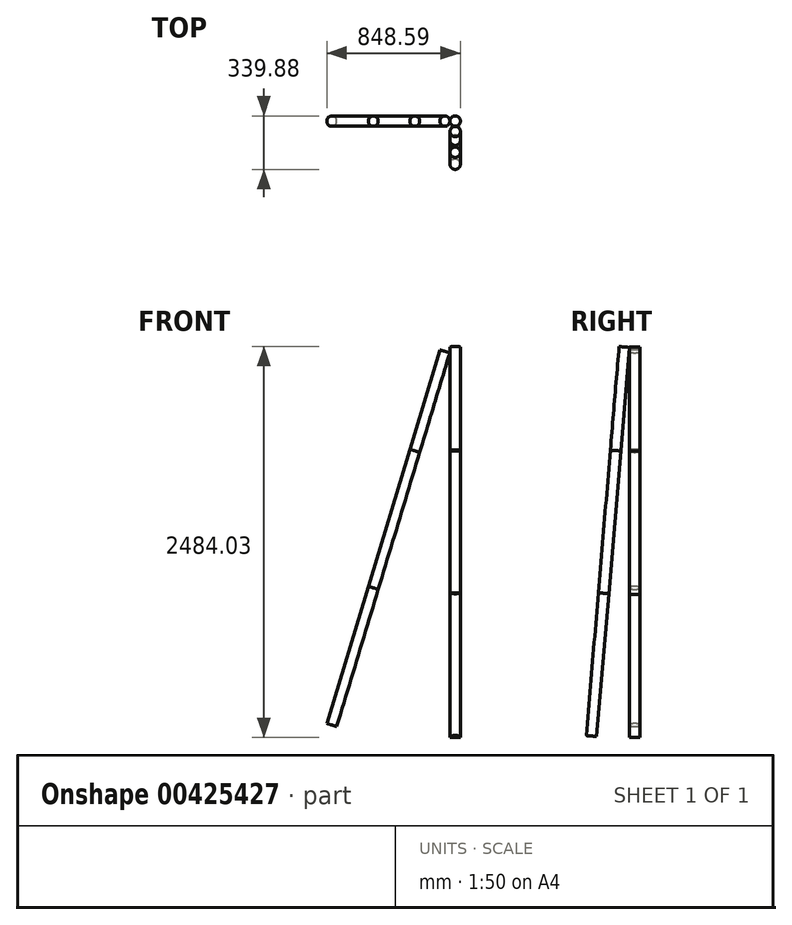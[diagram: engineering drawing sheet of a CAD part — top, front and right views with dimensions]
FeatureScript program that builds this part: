
annotation { "Feature Type Name" : "Feature", "Feature Type Description" : "" }
export const myFeature = defineFeature(function(context is Context, id is Id, definition is map)
    precondition{}
    {
        {
            assignVariable(context, id + "F0", {"name" : "A0RollLength", "anyValue" : 910 * mm});
        }
        {
            assignVariable(context, id + "F1", {"name" : "A1RollLength", "anyValue" : 660 * mm});
        }
        {
            var Q0;
            Q0=qCreatedBy(makeId("Top.planeOp"),FACE);
            var sketch = newSketch(context, id + "F2", { "sketchPlane" : qUnion([Q0])});
            skLineSegment(sketch, "E0.bottom", {"start": v(-465, 200) * mm, "end": v(465, 200) * mm});
            skLineSegment(sketch, "E0.top", {"start": v(-465, -200) * mm, "end": v(465, -200) * mm});
            skLineSegment(sketch, "E0.left", {"start": v(-465, 200) * mm, "end": v(-465, -200) * mm});
            skLineSegment(sketch, "E0.right", {"start": v(465, 200) * mm, "end": v(465, -200) * mm});
            skPoint(sketch, "E1", {"position": v(0, 200) * mm});
            skPoint(sketch, "E2", {"position": v(-465, 0) * mm});
            skCircle(sketch, "E3", {"center": v(392, 137) * mm, "radius": 33 * mm, "construction": true});
            skCircle(sketch, "E4", {"center": v(-402, 137) * mm, "radius": 33 * mm, "construction": true});
            skCircle(sketch, "E5", {"center": v(-402, -137) * mm, "radius": 33 * mm, "construction": true});
            skCircle(sketch, "E6", {"center": v(392, -137) * mm, "radius": 33 * mm, "construction": true});
            skLineSegment(sketch, "E7", {"start": v(-402, 137) * mm, "end": v(392, 137) * mm, "construction": true});
            skLineSegment(sketch, "E8", {"start": v(392, 137) * mm, "end": v(392, -137) * mm, "construction": true});
            skSolve(sketch);
        }
        {
            var Q0;
            Q0=sQuery(id+"F2.wireOp",EDGE,"E8");
            cPoint(context, id + "F3", {"entities" : qUnion([Q0]), "parameter" : 0.5});
        }
        {
            var Q0;
            Q0 = qCreatedBy(id + "F3" ,VERTEX);
            var Q1;
            Q1=qCreatedBy(makeId("Right.planeOp"),FACE);
            cPlane(context, id + "F4", {"entities" : qUnion([Q0, Q1]), "cplaneType" : CPlaneType.PLANE_POINT, "offset" : 253 * mm, "width" : 150 * mm, "height" : 150 * mm});
        }
        {
            var Q0;
            Q0=qCreatedBy(makeId("Front.planeOp"),FACE);
            var Q1;
            Q1=sQuery(id+"F2.wireOp",VERTEX,"E3.center");
            cPlane(context, id + "F5", {"entities" : qUnion([Q0, Q1]), "cplaneType" : CPlaneType.PLANE_POINT, "offset" : 25 * mm, "width" : 150 * mm, "height" : 150 * mm});
        }
        {
            var Q0;
            Q0=qCreatedBy(id+"F5.planeOp",FACE);
            var sketch = newSketch(context, id + "F6", { "sketchPlane" : qUnion([Q0])});
            skPoint(sketch, "E9.0", {"position": v(392, 0) * mm});
            skLineSegment(sketch, "E10", {"start": v(392, 0) * mm, "end": v(392, 2480) * mm, "construction": true});
            skPoint(sketch, "E11.0", {"position": v(-402, 0) * mm});
            skLineSegment(sketch, "E12", {"start": v(-392, 80) * mm, "end": v(326, 2453.79) * mm, "construction": true});
            skLineSegment(sketch, "E13", {"start": v(-423.59, 89.55) * mm, "end": v(-360.41, 70.45) * mm, "construction": true});
            skLineSegment(sketch, "E14", {"start": v(-435, 0) * mm, "end": v(-369, 0) * mm, "construction": true});
            skPoint(sketch, "E15", {"position": v(-363.28, 71.31) * mm});
            skSolve(sketch);
        }
        {
            var Q0;
            Q0=qCreatedBy(id+"F4.planeOp",FACE);
            var sketch = newSketch(context, id + "F7", { "sketchPlane" : qUnion([Q0])});
            skPoint(sketch, "E16.0", {"position": v(137, 0) * mm});
            skPoint(sketch, "E17.0", {"position": v(137, 2480) * mm});
            skPoint(sketch, "E18.0", {"position": v(-137, 0) * mm});
            skLineSegment(sketch, "E19", {"start": v(-137, 10) * mm, "end": v(71, 2481.26) * mm, "construction": true});
            skLineSegment(sketch, "E20", {"start": v(-169.88, 12.77) * mm, "end": v(-104.12, 7.23) * mm, "construction": true});
            skPoint(sketch, "E21", {"position": v(-107.1, 7.48) * mm});
            skSolve(sketch);
        }
        {
            var Q0;
            Q0=sQuery(id+"F6.wireOp",VERTEX,"E12.start");
            var Q1;
            Q1=sQuery(id+"F6.wireOp",EDGE,"E12");
            cPlane(context, id + "F8", {"entities" : qUnion([Q0, Q1]), "cplaneType" : CPlaneType.LINE_POINT, "offset" : 25 * mm, "width" : 150 * mm, "height" : 150 * mm});
        }
        {
            var Q0;
            Q0=sQuery(id+"F7.wireOp",EDGE,"E19");
            var Q1;
            Q1=sQuery(id+"F7.wireOp",VERTEX,"E19.start");
            cPlane(context, id + "F9", {"entities" : qUnion([Q0, Q1]), "cplaneType" : CPlaneType.LINE_POINT, "offset" : 25 * mm, "width" : 150 * mm, "height" : 150 * mm});
        }
        {
            var Q0;
            Q0=qCreatedBy(id+"F8.planeOp",FACE);
            var sketch = newSketch(context, id + "F10", { "sketchPlane" : qUnion([Q0])});
            skCircle(sketch, "E22", {"center": v(-398.37, 137) * mm, "radius": 33 * mm});
            skSolve(sketch);
        }
        {
            var Q0;
            Q0=makeQuery(id+"F10.imprint","IMPRINT",FACE,{"disambiguationData":[TD([[makeQuery(id+"F10.imprint","IMPRINT",EDGE,{"derivedFrom":sQuery(id+"F10.wireOp",EDGE,"E22")}),1.0]])]});
            extrude(context, id + "F11", {"entities" : qUnion([Q0]), "depth" : getVariable(context, 'A0RollLength')});
        }
        {
            var Q0;
            Q0=qCreatedBy(id+"F9.planeOp",FACE);
            var sketch = newSketch(context, id + "F12", { "sketchPlane" : qUnion([Q0])});
            skCircle(sketch, "E23", {"center": v(392, -137.36) * mm, "radius": 33 * mm});
            skSolve(sketch);
        }
        {
            var Q0;
            Q0=makeQuery(id+"F12.imprint","IMPRINT",FACE,{"disambiguationData":[TD([[makeQuery(id+"F12.imprint","IMPRINT",EDGE,{"derivedFrom":sQuery(id+"F12.wireOp",EDGE,"E23")}),1.0]])]});
            extrude(context, id + "F13", {"entities" : qUnion([Q0]), "depth" : getVariable(context, 'A0RollLength')});
        }
        {
            var Q0;
            Q0=qCreatedBy(makeId("Top.planeOp"),FACE);
            var sketch = newSketch(context, id + "F14", { "sketchPlane" : qUnion([Q0])});
            skCircle(sketch, "E24", {"center": v(392, 137) * mm, "radius": 33 * mm});
            skSolve(sketch);
        }
        {
            var Q0;
            Q0=makeQuery(id+"F14.imprint","IMPRINT",FACE,{"disambiguationData":[TD([[makeQuery(id+"F14.imprint","IMPRINT",EDGE,{"derivedFrom":sQuery(id+"F14.wireOp",EDGE,"E24")}),1.0]])]});
            extrude(context, id + "F15", {"entities" : qUnion([Q0]), "depth" : getVariable(context, 'A0RollLength')});
        }
        {
            var Q0;
            Q0=qCreatedBy(makeId("Top.planeOp"),FACE);
            cPlane(context, id + "F16", {"entities" : qUnion([Q0]), "cplaneType" : CPlaneType.OFFSET, "offset" : getVariable(context, 'A1RollLength'), "width" : 150 * mm, "height" : 150 * mm});
        }
        {
            var Q0;
            Q0=qCreatedBy(makeId("Top.planeOp"),FACE);
            cPlane(context, id + "F17", {"entities" : qUnion([Q0]), "cplaneType" : CPlaneType.OFFSET, "offset" : getVariable(context, 'A1RollLength') + getVariable(context, 'A1RollLength'), "width" : 150 * mm, "height" : 150 * mm});
        }
        {
            var Q0;
            Q0=qCreatedBy(makeId("Top.planeOp"),FACE);
            cPlane(context, id + "F18", {"entities" : qUnion([Q0]), "cplaneType" : CPlaneType.OFFSET, "offset" : 3 * getVariable(context, 'A1RollLength'), "width" : 150 * mm, "height" : 150 * mm});
        }
        {
            var Q0;
            Q0=makeQuery(id+"F11.opExtrude","CAP_FACE",FACE,{"disambiguationData":[OSD([sQuery(id+"F10.wireOp",EDGE,"E22")])],"isStart":false});
            extrude(context, id + "F19", {"entities" : qUnion([Q0]), "depth" : getVariable(context, 'A0RollLength')});
        }
        {
            var Q0;
            Q0=makeQuery(id+"F13.opExtrude","CAP_FACE",FACE,{"disambiguationData":[OSD([sQuery(id+"F12.wireOp",EDGE,"E23")])],"isStart":false});
            extrude(context, id + "F20", {"entities" : qUnion([Q0]), "depth" : getVariable(context, 'A0RollLength')});
        }
        {
            var Q0;
            Q0=makeQuery(id+"F15.opExtrude","CAP_FACE",FACE,{"disambiguationData":[OSD([sQuery(id+"F14.wireOp",EDGE,"E24")])],"isStart":false});
            extrude(context, id + "F21", {"entities" : qUnion([Q0]), "depth" : getVariable(context, 'A0RollLength')});
        }
        {
            var Q0;
            Q0=makeQuery(id+"F19.opExtrude","CAP_FACE",FACE,{"disambiguationData":[OSD([sQuery(id+"F10.wireOp",EDGE,"E22")])],"isStart":false});
            extrude(context, id + "F22", {"entities" : qUnion([Q0]), "depth" : getVariable(context, 'A1RollLength')});
        }
        {
            var Q0;
            Q0=makeQuery(id+"F20.opExtrude","CAP_FACE",FACE,{"disambiguationData":[OSD([sQuery(id+"F12.wireOp",EDGE,"E23")])],"isStart":false});
            extrude(context, id + "F23", {"entities" : qUnion([Q0]), "depth" : getVariable(context, 'A1RollLength')});
        }
        {
            var Q0;
            Q0=makeQuery(id+"F21.opExtrude","CAP_FACE",FACE,{"disambiguationData":[OSD([sQuery(id+"F14.wireOp",EDGE,"E24")])],"isStart":false});
            extrude(context, id + "F24", {"entities" : qUnion([Q0]), "depth" : getVariable(context, 'A1RollLength')});
        }
        {
            var Q0;
            Q0=qCreatedBy(makeId("Top.planeOp"),FACE);
            var Q1;
            Q1=sQuery(id+"F7.wireOp",VERTEX,"E17.0");
            cPlane(context, id + "F25", {"entities" : qUnion([Q0, Q1]), "cplaneType" : CPlaneType.PLANE_POINT, "offset" : 25 * mm, "width" : 150 * mm, "height" : 150 * mm});
        }
    });
